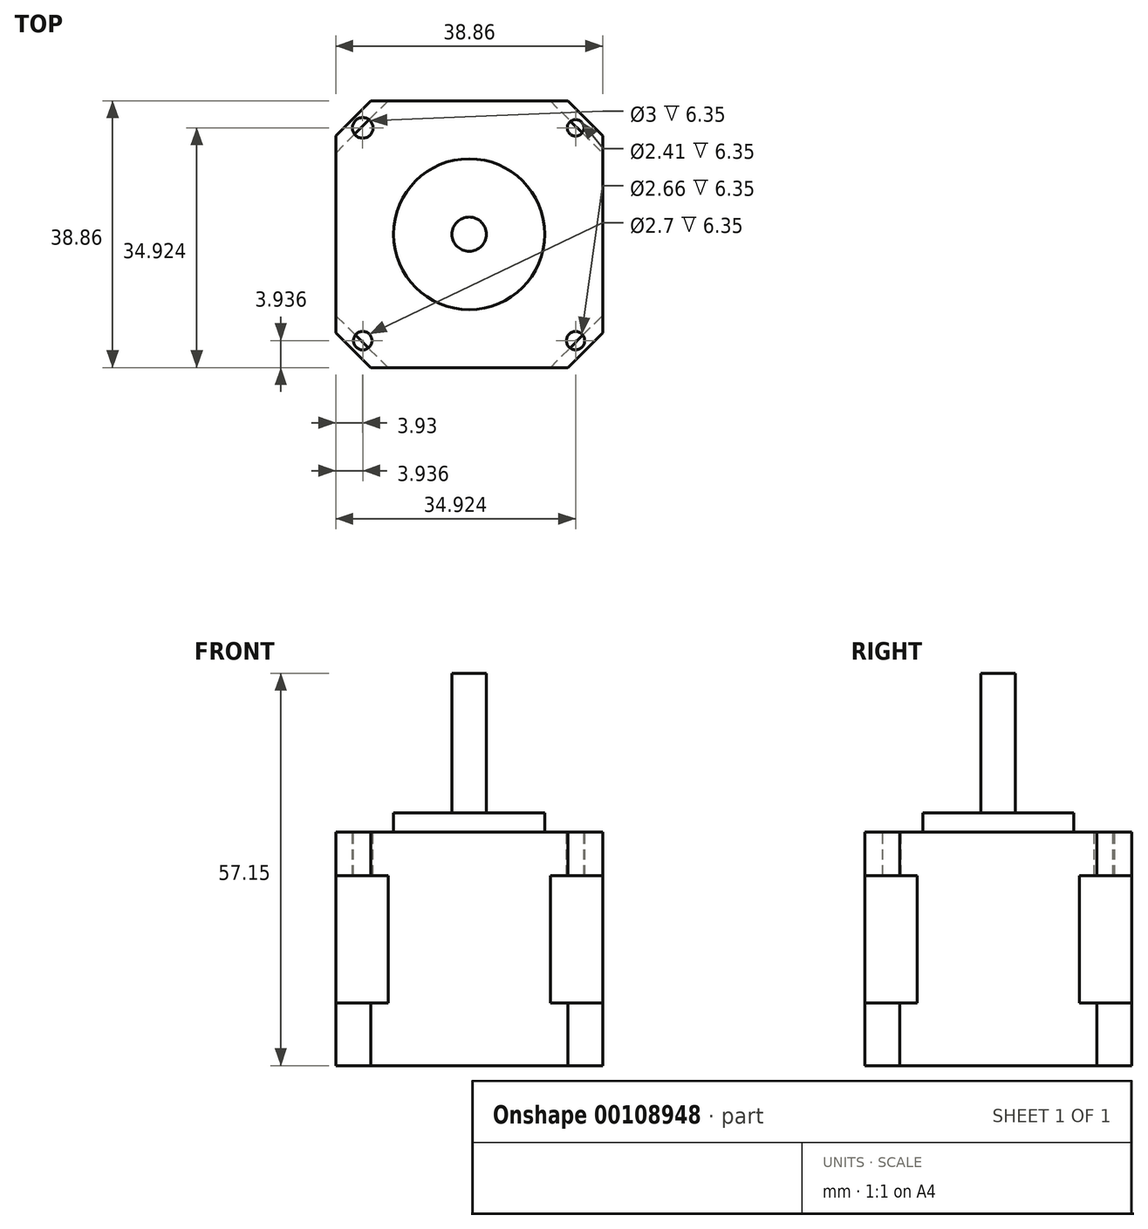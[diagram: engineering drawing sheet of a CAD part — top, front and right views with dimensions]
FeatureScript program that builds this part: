
annotation { "Feature Type Name" : "Feature", "Feature Type Description" : "" }
export const myFeature = defineFeature(function(context is Context, id is Id, definition is map)
    precondition{}
    {
        {
            var Q0;
            Q0=qCreatedBy(makeId("Top.planeOp"),FACE);
            var sketch = newSketch(context, id + "F0", { "sketchPlane" : qUnion([Q0])});
            skLineSegment(sketch, "E0.bottom", {"start": v(-19.43, 19.43) * mm, "end": v(19.43, 19.43) * mm});
            skLineSegment(sketch, "E0.top", {"start": v(-19.43, -19.43) * mm, "end": v(19.43, -19.43) * mm});
            skLineSegment(sketch, "E0.left", {"start": v(-19.43, 19.43) * mm, "end": v(-19.43, -19.43) * mm});
            skLineSegment(sketch, "E0.right", {"start": v(19.43, 19.43) * mm, "end": v(19.43, -19.43) * mm});
            skSolve(sketch);
        }
        {
            var Q0;
            Q0=makeQuery(id+"F0.imprint","IMPRINT",FACE,{"disambiguationData":[TD([[makeQuery(id+"F0.imprint","IMPRINT",EDGE,{"derivedFrom":sQuery(id+"F0.wireOp",EDGE,"E0.bottom")}),-1.0]])]});
            extrude(context, id + "F1", {"entities" : qUnion([Q0]), "endBound" : BoundingType.SYMMETRIC, "depth" : 21.34 * mm});
        }
        {
            var Q0;
            Q0=makeQuery(id+"F1.opExtrude","SWEPT_EDGE",EDGE,{"disambiguationData":[OSD([sQuery(id+"F0.wireOp",EDGE,"E0.bottom"),sQuery(id+"F0.wireOp",EDGE,"E0.right")])]});
            var Q1;
            Q1=makeQuery(id+"F1.opExtrude","SWEPT_EDGE",EDGE,{"disambiguationData":[OSD([sQuery(id+"F0.wireOp",EDGE,"E0.bottom"),sQuery(id+"F0.wireOp",EDGE,"E0.left")])]});
            var Q2;
            Q2=makeQuery(id+"F1.opExtrude","SWEPT_EDGE",EDGE,{"disambiguationData":[OSD([sQuery(id+"F0.wireOp",EDGE,"E0.top"),sQuery(id+"F0.wireOp",EDGE,"E0.left")])]});
            var Q3;
            Q3=makeQuery(id+"F1.opExtrude","SWEPT_EDGE",EDGE,{"disambiguationData":[OSD([sQuery(id+"F0.wireOp",EDGE,"E0.top"),sQuery(id+"F0.wireOp",EDGE,"E0.right")])]});
            chamfer(context, id + "F2", {"entities" : qUnion([Q0, Q1, Q2, Q3]), "width" : 7.62 * mm, "tangentPropagation" : true});
        }
        {
            var Q0;
            Q0=makeQuery(id+"F1.opExtrude","CAP_FACE",FACE,{"disambiguationData":[OSD([sQuery(id+"F0.wireOp",EDGE,"E0.bottom"),sQuery(id+"F0.wireOp",EDGE,"E0.top"),sQuery(id+"F0.wireOp",EDGE,"E0.left"),sQuery(id+"F0.wireOp",EDGE,"E0.right")])],"isStart":false});
            var sketch = newSketch(context, id + "F3", { "sketchPlane" : qUnion([Q0])});
            skLineSegment(sketch, "E1.bottom", {"start": v(-19.43, 19.43) * mm, "end": v(19.43, 19.43) * mm});
            skLineSegment(sketch, "E1.top", {"start": v(-19.43, -19.43) * mm, "end": v(19.43, -19.43) * mm});
            skLineSegment(sketch, "E1.left", {"start": v(-19.43, 19.43) * mm, "end": v(-19.43, -19.43) * mm});
            skLineSegment(sketch, "E1.right", {"start": v(19.43, 19.43) * mm, "end": v(19.43, -19.43) * mm});
            skSolve(sketch);
        }
        {
            var Q0;
            {var subQ0=sQuery(id+"F0.wireOp",EDGE,"E0.top");var subQ1=sQuery(id+"F0.wireOp",EDGE,"E0.right");var subQ2=sQuery(id+"F0.wireOp",EDGE,"E0.bottom");var subQ3=sQuery(id+"F0.wireOp",EDGE,"E0.left");var subQ4=makeQuery(id+"F1.opExtrude","CAP_FACE",FACE,{"disambiguationData":[OSD([subQ2,subQ0,subQ3,subQ1])],"isStart":false});var subQ8=makeQuery(id+"F2.opChamfer","BLEND_EDGE",EDGE,{"blendedFrom":[makeQuery(id+"F1.opExtrude","SWEPT_EDGE",EDGE,{"disambiguationData":[OSD([subQ2,subQ3])]}),subQ4],"blendedInto":[subQ4]});Q0=makeQuery(id+"F3.imprint","IMPRINT",FACE,{"disambiguationData":[TD([[makeQuery(id+"F3.imprint","IMPRINT",EDGE,{"derivedFrom":subQ8}),1.0]])]});}
            var Q1;
            {var subQ0=sQuery(id+"F0.wireOp",EDGE,"E0.bottom");var subQ1=sQuery(id+"F0.wireOp",EDGE,"E0.right");var subQ2=makeQuery(id+"F2.opChamfer","BLEND_EDGE",EDGE,{"blendedFrom":[makeQuery(id+"F1.opExtrude","SWEPT_EDGE",EDGE,{"disambiguationData":[OSD([subQ0,subQ1])]}),makeQuery(id+"F1.opExtrude","CAP_FACE",FACE,{"disambiguationData":[OSD([subQ0,sQuery(id+"F0.wireOp",EDGE,"E0.top"),sQuery(id+"F0.wireOp",EDGE,"E0.left"),subQ1])],"isStart":false})],"blendedInto":[makeQuery(id+"F1.opExtrude","CAP_FACE",FACE,{"disambiguationData":[OSD([subQ0,sQuery(id+"F0.wireOp",EDGE,"E0.top"),sQuery(id+"F0.wireOp",EDGE,"E0.left"),subQ1])],"isStart":false})]});Q1=makeQuery(id+"F3.imprint","IMPRINT",FACE,{"disambiguationData":[TD([[makeQuery(id+"F3.imprint","IMPRINT",EDGE,{"derivedFrom":subQ2}),-1.0]])]});}
            var Q2;
            {var subQ0=sQuery(id+"F0.wireOp",EDGE,"E0.bottom");var subQ1=sQuery(id+"F0.wireOp",EDGE,"E0.left");var subQ2=makeQuery(id+"F2.opChamfer","BLEND_EDGE",EDGE,{"blendedFrom":[makeQuery(id+"F1.opExtrude","SWEPT_EDGE",EDGE,{"disambiguationData":[OSD([subQ0,subQ1])]}),makeQuery(id+"F1.opExtrude","CAP_FACE",FACE,{"disambiguationData":[OSD([subQ0,sQuery(id+"F0.wireOp",EDGE,"E0.top"),subQ1,sQuery(id+"F0.wireOp",EDGE,"E0.right")])],"isStart":false})],"blendedInto":[makeQuery(id+"F1.opExtrude","CAP_FACE",FACE,{"disambiguationData":[OSD([subQ0,sQuery(id+"F0.wireOp",EDGE,"E0.top"),subQ1,sQuery(id+"F0.wireOp",EDGE,"E0.right")])],"isStart":false})]});Q2=makeQuery(id+"F3.imprint","IMPRINT",FACE,{"disambiguationData":[TD([[makeQuery(id+"F3.imprint","IMPRINT",EDGE,{"derivedFrom":subQ2}),-1.0]])]});}
            var Q3;
            {var subQ0=sQuery(id+"F0.wireOp",EDGE,"E0.top");var subQ1=sQuery(id+"F0.wireOp",EDGE,"E0.left");var subQ2=makeQuery(id+"F2.opChamfer","BLEND_EDGE",EDGE,{"blendedFrom":[makeQuery(id+"F1.opExtrude","SWEPT_EDGE",EDGE,{"disambiguationData":[OSD([subQ0,subQ1])]}),makeQuery(id+"F1.opExtrude","CAP_FACE",FACE,{"disambiguationData":[OSD([sQuery(id+"F0.wireOp",EDGE,"E0.bottom"),subQ0,subQ1,sQuery(id+"F0.wireOp",EDGE,"E0.right")])],"isStart":false})],"blendedInto":[makeQuery(id+"F1.opExtrude","CAP_FACE",FACE,{"disambiguationData":[OSD([sQuery(id+"F0.wireOp",EDGE,"E0.bottom"),subQ0,subQ1,sQuery(id+"F0.wireOp",EDGE,"E0.right")])],"isStart":false})]});Q3=makeQuery(id+"F3.imprint","IMPRINT",FACE,{"disambiguationData":[TD([[makeQuery(id+"F3.imprint","IMPRINT",EDGE,{"derivedFrom":subQ2}),-1.0]])]});}
            var Q4;
            {var subQ0=sQuery(id+"F0.wireOp",EDGE,"E0.top");var subQ1=sQuery(id+"F0.wireOp",EDGE,"E0.right");var subQ2=makeQuery(id+"F2.opChamfer","BLEND_EDGE",EDGE,{"blendedFrom":[makeQuery(id+"F1.opExtrude","SWEPT_EDGE",EDGE,{"disambiguationData":[OSD([subQ0,subQ1])]}),makeQuery(id+"F1.opExtrude","CAP_FACE",FACE,{"disambiguationData":[OSD([sQuery(id+"F0.wireOp",EDGE,"E0.bottom"),subQ0,sQuery(id+"F0.wireOp",EDGE,"E0.left"),subQ1])],"isStart":false})],"blendedInto":[makeQuery(id+"F1.opExtrude","CAP_FACE",FACE,{"disambiguationData":[OSD([sQuery(id+"F0.wireOp",EDGE,"E0.bottom"),subQ0,sQuery(id+"F0.wireOp",EDGE,"E0.left"),subQ1])],"isStart":false})]});Q4=makeQuery(id+"F3.imprint","IMPRINT",FACE,{"disambiguationData":[TD([[makeQuery(id+"F3.imprint","IMPRINT",EDGE,{"derivedFrom":subQ2}),-1.0]])]});}
            extrude(context, id + "F4", {"entities" : qUnion([Q0, Q1, Q2, Q3, Q4]), "operationType" : NewBodyOperationType.ADD, "depth" : 6.35 * mm});
        }
        {
            var Q0;
            Q0=makeQuery(id+"F4.opExtrude","SWEPT_EDGE",EDGE,{"disambiguationData":[OSD([sQuery(id+"F3.wireOp",EDGE,"E1.bottom"),sQuery(id+"F3.wireOp",EDGE,"E1.right")])]});
            var Q1;
            Q1=makeQuery(id+"F4.opExtrude","SWEPT_EDGE",EDGE,{"disambiguationData":[OSD([sQuery(id+"F3.wireOp",EDGE,"E1.bottom"),sQuery(id+"F3.wireOp",EDGE,"E1.left")])]});
            var Q2;
            Q2=makeQuery(id+"F4.opExtrude","SWEPT_EDGE",EDGE,{"disambiguationData":[OSD([sQuery(id+"F3.wireOp",EDGE,"E1.top"),sQuery(id+"F3.wireOp",EDGE,"E1.left")])]});
            var Q3;
            Q3=makeQuery(id+"F4.opExtrude","SWEPT_EDGE",EDGE,{"disambiguationData":[OSD([sQuery(id+"F3.wireOp",EDGE,"E1.top"),sQuery(id+"F3.wireOp",EDGE,"E1.right")])]});
            chamfer(context, id + "F5", {"entities" : qUnion([Q0, Q1, Q2, Q3]), "width" : 5.08 * mm, "tangentPropagation" : true});
        }
        {
            var Q0;
            Q0=makeQuery(id+"F1.opExtrude","CAP_FACE",FACE,{"disambiguationData":[OSD([sQuery(id+"F0.wireOp",EDGE,"E0.bottom"),sQuery(id+"F0.wireOp",EDGE,"E0.top"),sQuery(id+"F0.wireOp",EDGE,"E0.left"),sQuery(id+"F0.wireOp",EDGE,"E0.right")])],"isStart":true});
            var sketch = newSketch(context, id + "F6", { "sketchPlane" : qUnion([Q0])});
            skLineSegment(sketch, "E2.0.0", {"start": v(-14.35, 19.43) * mm, "end": v(14.35, 19.43) * mm});
            skLineSegment(sketch, "E2.0.1", {"start": v(14.35, 19.43) * mm, "end": v(19.43, 14.35) * mm});
            skLineSegment(sketch, "E2.0.2", {"start": v(19.43, -14.35) * mm, "end": v(19.43, 14.35) * mm});
            skLineSegment(sketch, "E2.0.3", {"start": v(19.43, -14.35) * mm, "end": v(14.35, -19.43) * mm});
            skLineSegment(sketch, "E2.0.4", {"start": v(-14.35, -19.43) * mm, "end": v(14.35, -19.43) * mm});
            skLineSegment(sketch, "E2.0.5", {"start": v(-14.35, -19.43) * mm, "end": v(-19.43, -14.35) * mm});
            skLineSegment(sketch, "E2.0.6", {"start": v(-19.43, -14.35) * mm, "end": v(-19.43, 14.35) * mm});
            skLineSegment(sketch, "E2.0.7", {"start": v(-19.43, 14.35) * mm, "end": v(-14.35, 19.43) * mm});
            skSolve(sketch);
        }
        {
            var Q0;
            {var subQ3=sQuery(id+"F6.wireOp",EDGE,"E2.0.7");Q0=makeQuery(id+"F6.imprint","IMPRINT",FACE,{"disambiguationData":[TD([[makeQuery(id+"F6.imprint","IMPRINT",EDGE,{"derivedFrom":subQ3}),-1.0]])]});}
            var Q1;
            {var subQ4=sQuery(id+"F6.wireOp",EDGE,"E2.0.1");Q1=makeQuery(id+"F6.imprint","IMPRINT",FACE,{"disambiguationData":[TD([[makeQuery(id+"F6.imprint","IMPRINT",EDGE,{"derivedFrom":subQ4}),-1.0]])]});}
            var Q2;
            {var subQ4=sQuery(id+"F6.wireOp",EDGE,"E2.0.3");Q2=makeQuery(id+"F6.imprint","IMPRINT",FACE,{"disambiguationData":[TD([[makeQuery(id+"F6.imprint","IMPRINT",EDGE,{"derivedFrom":subQ4}),-1.0]])]});}
            var Q3;
            {var subQ4=sQuery(id+"F6.wireOp",EDGE,"E2.0.5");Q3=makeQuery(id+"F6.imprint","IMPRINT",FACE,{"disambiguationData":[TD([[makeQuery(id+"F6.imprint","IMPRINT",EDGE,{"derivedFrom":subQ4}),-1.0]])]});}
            var Q4;
            {var subQ0=sQuery(id+"F0.wireOp",EDGE,"E0.top");var subQ1=sQuery(id+"F0.wireOp",EDGE,"E0.right");var subQ2=sQuery(id+"F0.wireOp",EDGE,"E0.bottom");var subQ3=sQuery(id+"F0.wireOp",EDGE,"E0.left");var subQ4=makeQuery(id+"F1.opExtrude","CAP_FACE",FACE,{"disambiguationData":[OSD([subQ2,subQ0,subQ3,subQ1])],"isStart":true});var subQ8=makeQuery(id+"F2.opChamfer","BLEND_EDGE",EDGE,{"blendedFrom":[makeQuery(id+"F1.opExtrude","SWEPT_EDGE",EDGE,{"disambiguationData":[OSD([subQ2,subQ3])]}),subQ4],"blendedInto":[subQ4]});Q4=makeQuery(id+"F6.imprint","IMPRINT",FACE,{"disambiguationData":[TD([[makeQuery(id+"F6.imprint","IMPRINT",EDGE,{"derivedFrom":subQ8}),1.0]])]});}
            var Q5;
            Q5 = qSketchRegion(id + "F8", true);
            extrude(context, id + "F7", {"entities" : qUnion([Q0, Q1, Q2, Q3, Q4, Q5]), "operationType" : NewBodyOperationType.ADD, "depth" : 6.35 * mm});
        }
        {
            var Q0;
            Q0=makeQuery(id+"F4.opExtrude","CAP_FACE",FACE,{"disambiguationData":[OSD([sQuery(id+"F3.wireOp",EDGE,"E1.bottom"),sQuery(id+"F3.wireOp",EDGE,"E1.top"),sQuery(id+"F3.wireOp",EDGE,"E1.left"),sQuery(id+"F3.wireOp",EDGE,"E1.right")])],"isStart":false});
            var sketch = newSketch(context, id + "F8", { "sketchPlane" : qUnion([Q0])});
            skCircle(sketch, "E3", {"center": v(0, 0) * mm, "radius": 11 * mm});
            skSolve(sketch);
        }
        {
            var Q0;
            Q0 = qSketchRegion(id + "F8", true);
            var Q1;
            Q1 = qSketchRegion(id + "F6", true);
            extrude(context, id + "F9", {"entities" : qUnion([Q0, Q1]), "operationType" : NewBodyOperationType.ADD, "depth" : 2.8 * mm});
        }
        {
            var Q0;
            Q0=makeQuery(id+"F9.opExtrude","CAP_FACE",FACE,{"disambiguationData":[OSD([sQuery(id+"F8.wireOp",EDGE,"E3")])],"isStart":false});
            var sketch = newSketch(context, id + "F10", { "sketchPlane" : qUnion([Q0])});
            skCircle(sketch, "E4", {"center": v(0, 0) * mm, "radius": 2.5 * mm});
            skSolve(sketch);
        }
        {
            var Q0;
            Q0=makeQuery(id+"F10.imprint","IMPRINT",FACE,{"disambiguationData":[TD([[makeQuery(id+"F10.imprint","IMPRINT",EDGE,{"derivedFrom":sQuery(id+"F10.wireOp",EDGE,"E4")}),1.0]])]});
            extrude(context, id + "F11", {"entities" : qUnion([Q0]), "operationType" : NewBodyOperationType.ADD, "depth" : 20.32 * mm});
        }
        {
            var Q0;
            Q0=makeQuery(id+"F11.opExtrude","CAP_FACE",FACE,{"disambiguationData":[OSD([sQuery(id+"F10.wireOp",EDGE,"E4")])],"isStart":false});
            var sketch = newSketch(context, id + "F12", { "sketchPlane" : qUnion([Q0])});
            skLineSegment(sketch, "E5.bottom", {"start": v(-6.57, 7.33) * mm, "end": v(6.56, 7.33) * mm});
            skLineSegment(sketch, "E5.top", {"start": v(-6.57, 5) * mm, "end": v(6.56, 5) * mm});
            skLineSegment(sketch, "E5.left", {"start": v(-6.57, 7.33) * mm, "end": v(-6.57, 5) * mm});
            skLineSegment(sketch, "E5.right", {"start": v(6.56, 7.33) * mm, "end": v(6.56, 5) * mm});
            skSolve(sketch);
        }
        {
            var Q0;
            {var subQ0=makeQuery(id+"F11.opExtrude","CAP_EDGE",EDGE,{"disambiguationData":[OSD([sQuery(id+"F10.wireOp",EDGE,"E4")])],"isStart":false});var subQ1=sQuery(id+"F12.wireOp",EDGE,"E5.top");var subQ3=makeQuery(id+"F12.imprint","INTERSECT",VERTEX,{"disambiguationData":[OD(0.0)],"derivedFrom":[subQ0,subQ1]});Q0=qUnion([makeQuery(id+"F12.imprint","IMPRINT",FACE,{"disambiguationData":[TD([[makeQuery(id+"F12.imprint","IMPRINT",EDGE,{"derivedFrom":sQuery(id+"F12.wireOp",EDGE,"E5.bottom")}),-1.0]])]}),makeQuery(id+"F12.imprint","IMPRINT",FACE,{"disambiguationData":[TD([[makeQuery(id+"F12.imprint","IMPRINT",EDGE,{"disambiguationData":[TD([[subQ3,-1.0]])],"derivedFrom":subQ1}),1.0]])]})]);}
            extrude(context, id + "F13", {"entities" : qUnion([Q0]), "operationType" : NewBodyOperationType.REMOVE, "oppositeDirection" : true, "depth" : 10.16 * mm});
        }
        {
            var Q0;
            Q0=makeQuery(id+"F4.opExtrude","CAP_FACE",FACE,{"disambiguationData":[OSD([sQuery(id+"F3.wireOp",EDGE,"E1.bottom"),sQuery(id+"F3.wireOp",EDGE,"E1.top"),sQuery(id+"F3.wireOp",EDGE,"E1.left"),sQuery(id+"F3.wireOp",EDGE,"E1.right")])],"isStart":false});
            var sketch = newSketch(context, id + "F14", { "sketchPlane" : qUnion([Q0])});
            skCircle(sketch, "E6", {"center": v(-15.5, 15.5) * mm, "radius": 1.5 * mm});
            skCircle(sketch, "E7", {"center": v(15.5, 15.5) * mm, "radius": 1.2 * mm});
            skCircle(sketch, "E8", {"center": v(15.5, -15.5) * mm, "radius": 1.33 * mm});
            skCircle(sketch, "E9", {"center": v(-15.5, -15.5) * mm, "radius": 1.35 * mm});
            skSolve(sketch);
        }
        {
            var Q0;
            {Q0=qUnion([makeQuery(id+"F14.imprint","IMPRINT",FACE,{"disambiguationData":[TD([[makeQuery(id+"F14.imprint","IMPRINT",EDGE,{"derivedFrom":sQuery(id+"F14.wireOp",EDGE,"E6")}),1.0]])]}),makeQuery(id+"F14.imprint","IMPRINT",FACE,{"disambiguationData":[TD([[makeQuery(id+"F14.imprint","IMPRINT",EDGE,{"derivedFrom":sQuery(id+"F14.wireOp",EDGE,"E7")}),1.0]])]}),makeQuery(id+"F14.imprint","IMPRINT",FACE,{"disambiguationData":[TD([[makeQuery(id+"F14.imprint","IMPRINT",EDGE,{"derivedFrom":sQuery(id+"F14.wireOp",EDGE,"E8")}),1.0]])]}),makeQuery(id+"F14.imprint","IMPRINT",FACE,{"disambiguationData":[TD([[makeQuery(id+"F14.imprint","IMPRINT",EDGE,{"derivedFrom":sQuery(id+"F14.wireOp",EDGE,"E9")}),1.0]])]})]);}
            extrude(context, id + "F15", {"entities" : qUnion([Q0]), "operationType" : NewBodyOperationType.REMOVE, "oppositeDirection" : true, "depth" : 6.35 * mm});
        }
    });
